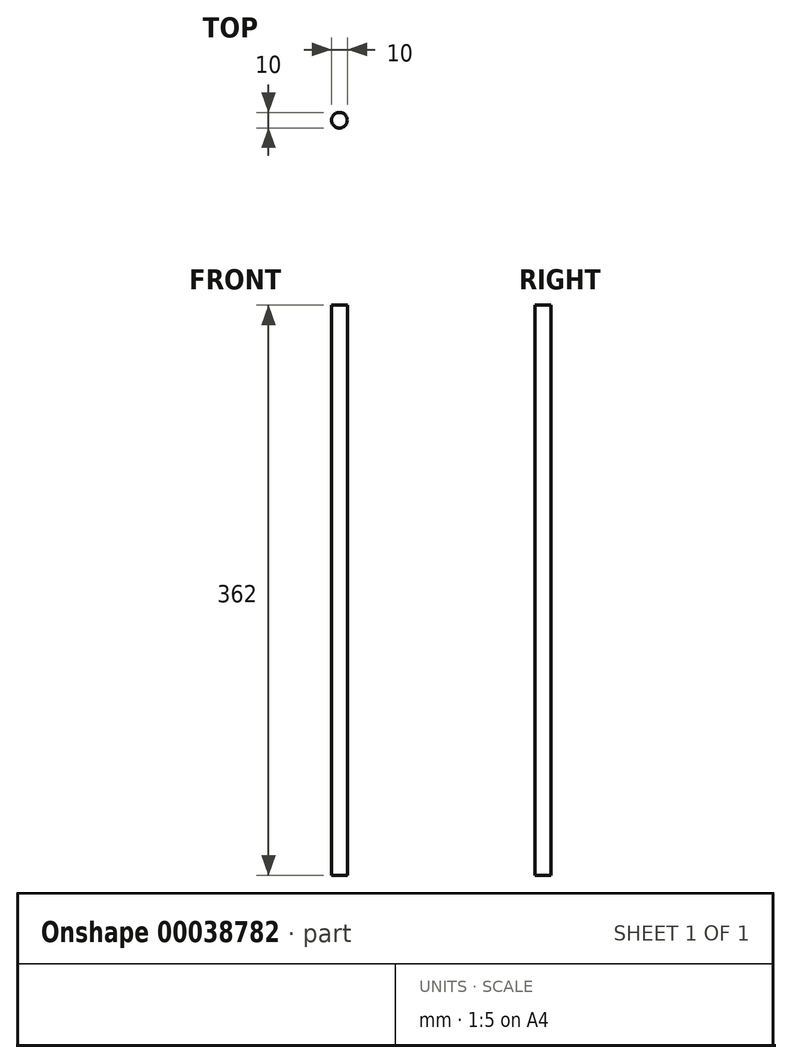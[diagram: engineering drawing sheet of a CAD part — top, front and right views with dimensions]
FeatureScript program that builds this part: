
annotation { "Feature Type Name" : "Feature", "Feature Type Description" : "" }
export const myFeature = defineFeature(function(context is Context, id is Id, definition is map)
    precondition{}
    {
        {
            var Q0;
            Q0=qCreatedBy(makeId("Top.planeOp"),FACE);
            var sketch = newSketch(context, id + "F0", { "sketchPlane" : qUnion([Q0])});
            skCircle(sketch, "E0", {"center": v(0, 0) * mm, "radius": 5 * mm});
            skSolve(sketch);
        }
        {
            var Q0;
            Q0=qSketchRegion(id+"F0",true);
            extrude(context, id + "F1", {"entities" : qUnion([Q0]), "depth" : 362 * mm});
        }
    });
